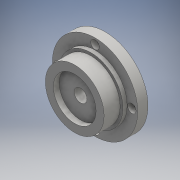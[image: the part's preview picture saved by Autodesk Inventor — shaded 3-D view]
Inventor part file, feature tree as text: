
AUTODESK INVENTOR PART (.ipt)
format: ipt  version: 2016 (Build 200138000, 138)  size: 169,472 bytes
history: native  units: mm
features: extrude x6, sketch x6, hole x4, other x1
ambient origin geometry x8: Origin, YZ Plane, XZ Plane, XY Plane, X Axis, Y Axis, Z Axis, Center Point
bodies: Body1 (feature_tree)
feature tree (17):
  other  "ソリッド1"
  extrude  "押し出し1"  Depth=80.0mm
  extrude  "押し出し2"  Depth=28.6mm TaperAngle=0.0deg
  extrude  "押し出し3"  Depth=60.1mm
  extrude  "押し出し4"  Depth=80.0mm
  extrude  "押し出し5"  Depth=19.0mm TaperAngle=0.0deg
  extrude  "押し出し6"  Depth=55.0mm
  hole  "穴1"  [1 undecoded]
  hole  "穴2"  [1 undecoded]
  hole  "穴3"  [1 undecoded]
  hole  "穴4"  [1 undecoded]
  sketch  "スケッチ1"
  sketch  "スケッチ2"
  sketch  "スケッチ3"
  sketch  "スケッチ5"
  sketch  "スケッチ6"
  sketch  "スケッチ7"
note: 4 required parameter values undecoded (feature->parameter linkage not recoverable at this tier; creation-order binding heuristic only, values carry confidence <= 0.55)
